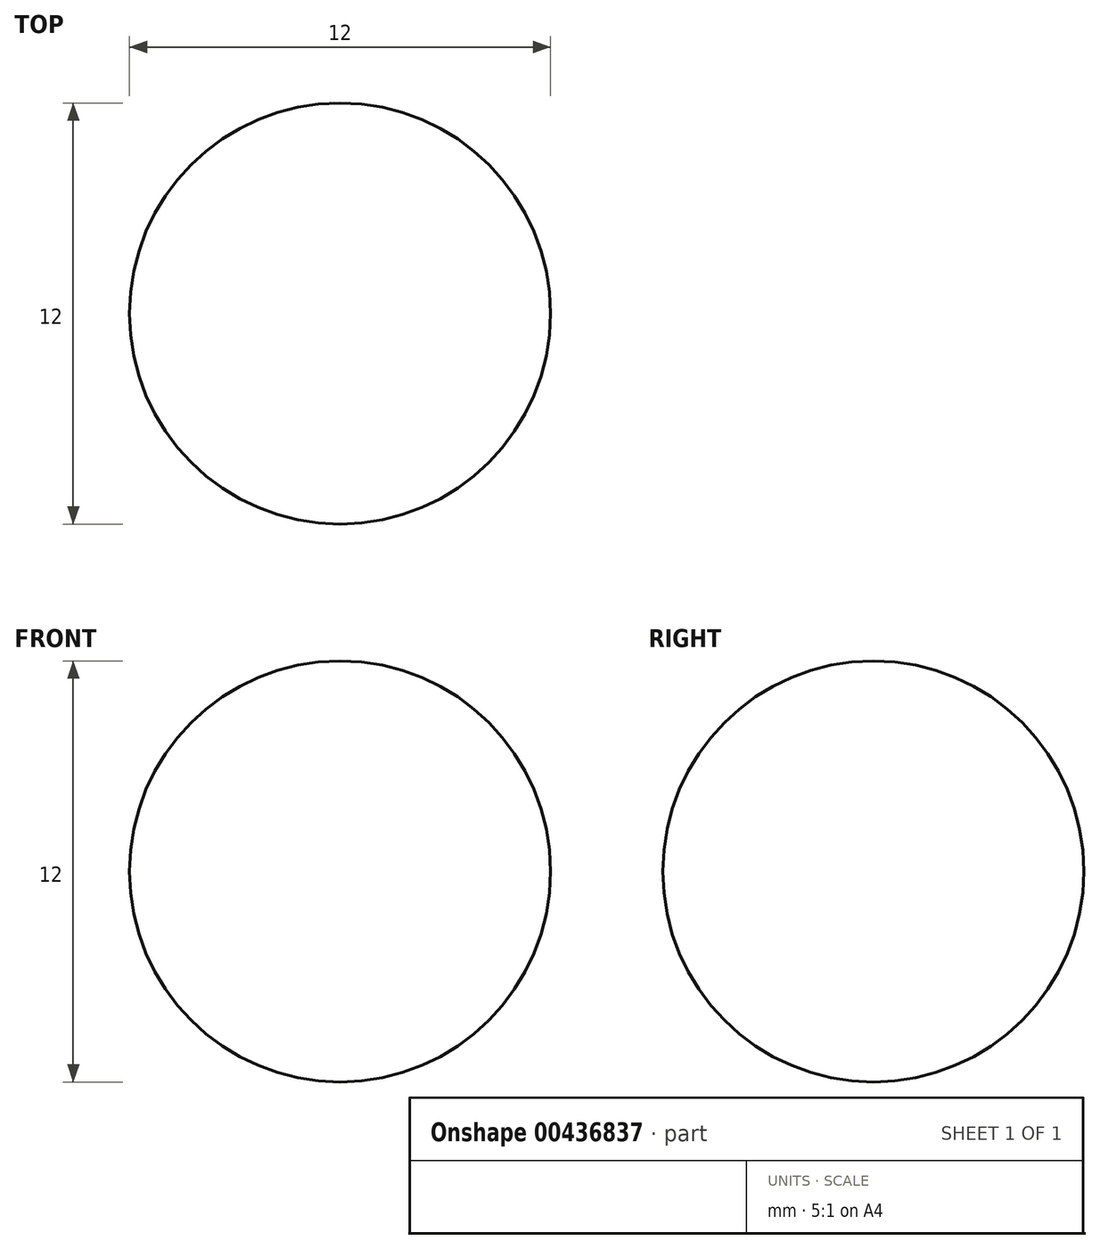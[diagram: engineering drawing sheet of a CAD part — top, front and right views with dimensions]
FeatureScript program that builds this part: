
annotation { "Feature Type Name" : "Feature", "Feature Type Description" : "" }
export const myFeature = defineFeature(function(context is Context, id is Id, definition is map)
    precondition{}
    {
        {
            var Q0;
            Q0=qCreatedBy(makeId("Front.planeOp"),FACE);
            var sketch = newSketch(context, id + "F0", { "sketchPlane" : qUnion([Q0])});
            skArc(sketch, "E0", {"start": v(0, -6) * mm, "mid": v(6, 0) * mm, "end": v(0, 6) * mm});
            skLineSegment(sketch, "E1", {"start": v(0, 6) * mm, "end": v(0, -6) * mm});
            skSolve(sketch);
        }
        {
            var Q0;
            Q0=makeQuery(id+"F0.imprint","IMPRINT",FACE,{"disambiguationData":[TD([[makeQuery(id+"F0.imprint","IMPRINT",EDGE,{"derivedFrom":sQuery(id+"F0.wireOp",EDGE,"E0")}),1.0]])]});
            var Q1;
            Q1=sQuery(id+"F0.wireOp",EDGE,"E1");
            revolve(context, id + "F1", {"entities" : qUnion([Q0]), "axis" : qUnion([Q1]), "revolveType" : RevolveType.FULL});
        }
    });
